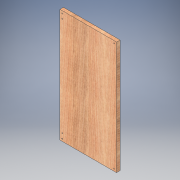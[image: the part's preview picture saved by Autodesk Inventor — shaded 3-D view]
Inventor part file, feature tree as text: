
AUTODESK INVENTOR PART (.ipt)
format: ipt  version: 2018 (Build 220112000, 112)  size: 141,824 bytes
history: native  units: in
note: dims shown in document units (in); Inventor stores cm internally (conversion verified against a paired STEP export)
features: extrude x2, sketch x2
ambient origin geometry x8: Origin, YZ Plane, XZ Plane, XY Plane, X Axis, Y Axis, Z Axis, Center Point
bodies: Solid1 (feature_tree)
feature tree (4):
  extrude  "Extrusion1"  Depth=24.0in
  extrude  "Extrusion3"  Depth=0.75in
  sketch  "Sketch1"  dims[d0=12.0in d1=24.0in]
  sketch  "Sketch2"  dims[d2=0.75in d3=0.0in d4=0.5in d5=0.5in d6=0.5in d7=0.5in d8=0.2031in d11=1.0in d12=0.75in d13=0.0in]
